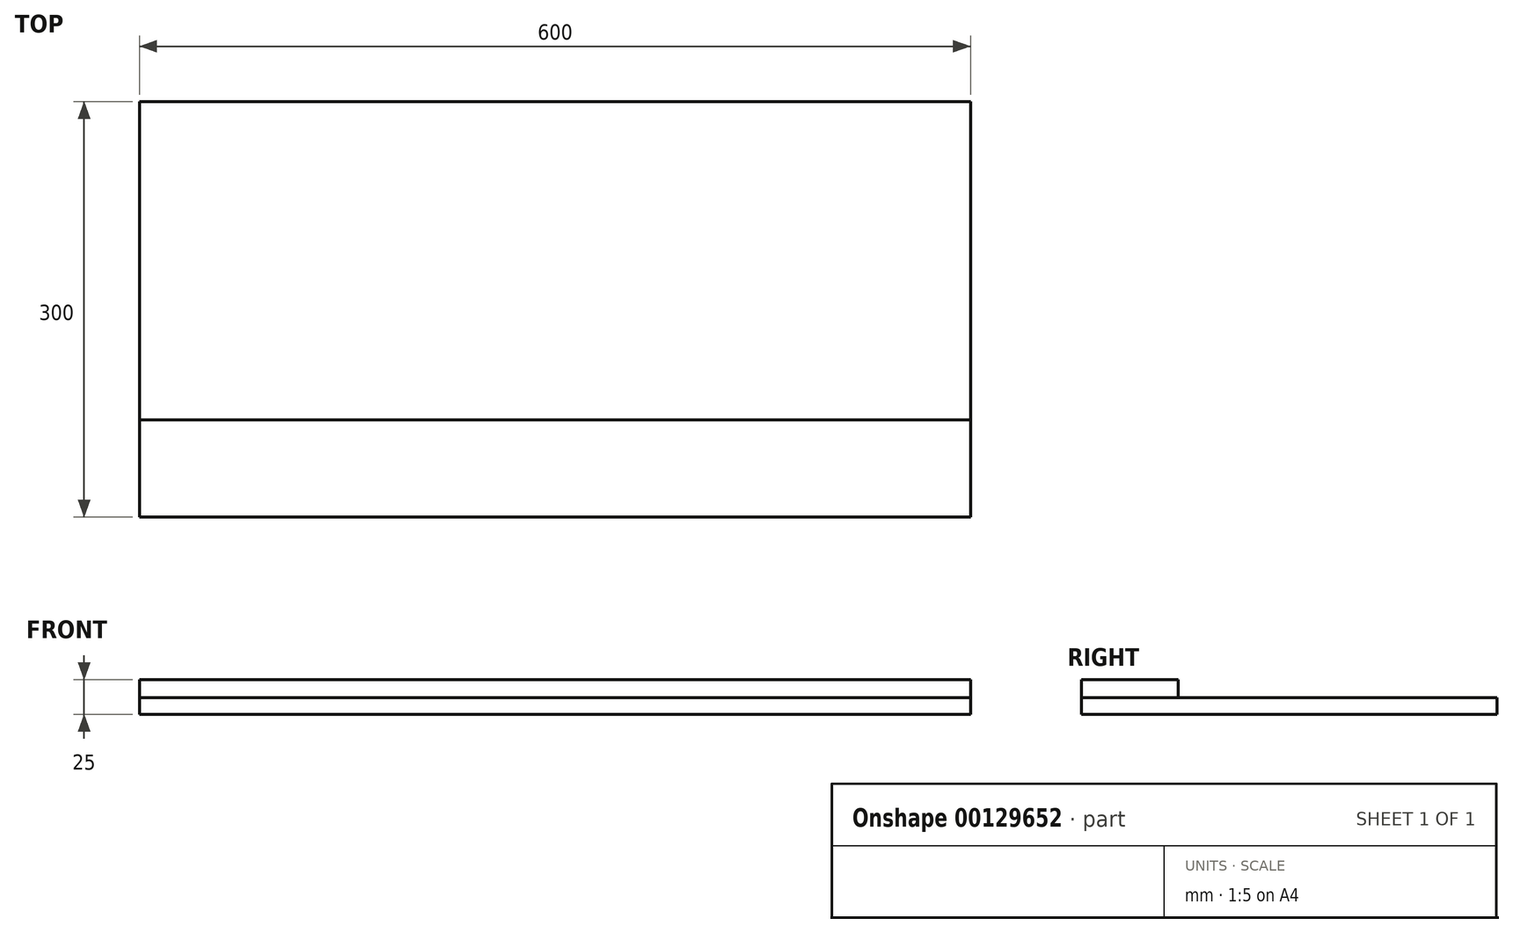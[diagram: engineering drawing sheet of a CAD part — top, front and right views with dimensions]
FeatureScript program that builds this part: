
annotation { "Feature Type Name" : "Feature", "Feature Type Description" : "" }
export const myFeature = defineFeature(function(context is Context, id is Id, definition is map)
    precondition{}
    {
        {
            var Q0;
            Q0=qCreatedBy(makeId("Top.planeOp"),FACE);
            var sketch = newSketch(context, id + "F0", { "sketchPlane" : qUnion([Q0])});
            skLineSegment(sketch, "E0.bottom", {"start": v(0, 0) * mm, "end": v(600, 0) * mm});
            skLineSegment(sketch, "E0.top", {"start": v(0, 300) * mm, "end": v(600, 300) * mm});
            skLineSegment(sketch, "E0.left", {"start": v(0, 0) * mm, "end": v(0, 300) * mm});
            skLineSegment(sketch, "E0.right", {"start": v(600, 0) * mm, "end": v(600, 300) * mm});
            skSolve(sketch);
        }
        {
            var Q0;
            Q0=makeQuery(id+"F0.imprint","IMPRINT",FACE,{"disambiguationData":[TD([[makeQuery(id+"F0.imprint","IMPRINT",EDGE,{"derivedFrom":sQuery(id+"F0.wireOp",EDGE,"E0.bottom")}),1.0]])]});
            extrude(context, id + "F1", {"entities" : qUnion([Q0]), "depth" : 12 * mm});
        }
        {
            var Q0;
            Q0=makeQuery(id+"F1.opExtrude","CAP_FACE",FACE,{"disambiguationData":[OSD([sQuery(id+"F0.wireOp",EDGE,"E0.bottom"),sQuery(id+"F0.wireOp",EDGE,"E0.top"),sQuery(id+"F0.wireOp",EDGE,"E0.left"),sQuery(id+"F0.wireOp",EDGE,"E0.right")])],"isStart":false});
            var sketch = newSketch(context, id + "F2", { "sketchPlane" : qUnion([Q0])});
            skLineSegment(sketch, "E1.bottom", {"start": v(0, 0) * mm, "end": v(600, 0) * mm});
            skLineSegment(sketch, "E1.top", {"start": v(0, 70) * mm, "end": v(600, 70) * mm});
            skLineSegment(sketch, "E1.left", {"start": v(0, 0) * mm, "end": v(0, 70) * mm});
            skLineSegment(sketch, "E1.right", {"start": v(600, 0) * mm, "end": v(600, 70) * mm});
            skLineSegment(sketch, "E2.bottom", {"start": v(0, 76.6) * mm, "end": v(600, 76.6) * mm});
            skLineSegment(sketch, "E2.top", {"start": v(0, 146.6) * mm, "end": v(600, 146.6) * mm});
            skLineSegment(sketch, "E2.left", {"start": v(0, 76.6) * mm, "end": v(0, 146.6) * mm});
            skLineSegment(sketch, "E2.right", {"start": v(600, 76.6) * mm, "end": v(600, 146.6) * mm});
            skLineSegment(sketch, "E3.bottom", {"start": v(0, 153.4) * mm, "end": v(600, 153.4) * mm});
            skLineSegment(sketch, "E3.top", {"start": v(0, 223.4) * mm, "end": v(600, 223.4) * mm});
            skLineSegment(sketch, "E3.left", {"start": v(0, 153.4) * mm, "end": v(0, 223.4) * mm});
            skLineSegment(sketch, "E3.right", {"start": v(600, 153.4) * mm, "end": v(600, 223.4) * mm});
            skLineSegment(sketch, "E4.bottom", {"start": v(0, 300) * mm, "end": v(600, 300) * mm});
            skLineSegment(sketch, "E4.top", {"start": v(0, 230) * mm, "end": v(600, 230) * mm});
            skLineSegment(sketch, "E4.left", {"start": v(0, 300) * mm, "end": v(0, 230) * mm});
            skLineSegment(sketch, "E4.right", {"start": v(600, 300) * mm, "end": v(600, 230) * mm});
            skSolve(sketch);
        }
        {
            var Q0;
            Q0=makeQuery(id+"F2.imprint","IMPRINT",FACE,{"disambiguationData":[TD([[makeQuery(id+"F2.imprint","IMPRINT",EDGE,{"derivedFrom":sQuery(id+"F2.wireOp",EDGE,"E1.bottom")}),1.0]])]});
            extrude(context, id + "F3", {"entities" : qUnion([Q0]), "depth" : 13 * mm});
        }
    });
